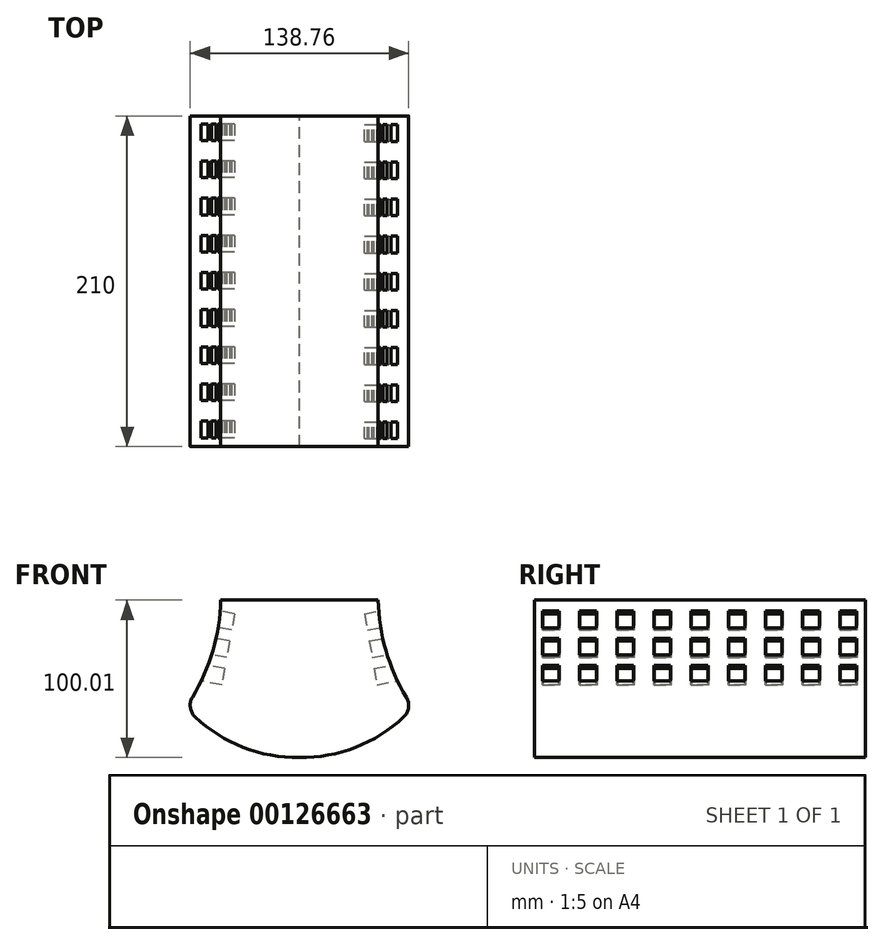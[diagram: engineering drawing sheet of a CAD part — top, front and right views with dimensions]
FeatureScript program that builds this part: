
annotation { "Feature Type Name" : "Feature", "Feature Type Description" : "" }
export const myFeature = defineFeature(function(context is Context, id is Id, definition is map)
    precondition{}
    {
        {
            var Q0;
            Q0=qCreatedBy(makeId("Front.planeOp"),FACE);
            var sketch = newSketch(context, id + "F0", { "sketchPlane" : qUnion([Q0])});
            skLineSegment(sketch, "E0", {"start": v(0, 100) * mm, "end": v(50, 100) * mm});
            skArc(sketch, "E1", {"start": v(50, 100) * mm, "mid": v(56.03, 64.31) * mm, "end": v(72.09, 31.88) * mm});
            skArc(sketch, "E2", {"start": v(0, 0) * mm, "mid": v(39.53, 8.06) * mm, "end": v(72.09, 31.88) * mm});
            skLineSegment(sketch, "E3", {"start": v(0, 100) * mm, "end": v(-50, 100) * mm});
            skArc(sketch, "E4", {"start": v(-72.09, 31.88) * mm, "mid": v(-56.03, 64.31) * mm, "end": v(-50, 100) * mm});
            skArc(sketch, "E5", {"start": v(-72.09, 31.88) * mm, "mid": v(-39.53, 8.06) * mm, "end": v(0, 0) * mm});
            skSolve(sketch);
        }
        {
            var Q0;
            Q0=makeQuery(id+"F0.imprint","IMPRINT",FACE,{"disambiguationData":[TD([[makeQuery(id+"F0.imprint","IMPRINT",EDGE,{"derivedFrom":sQuery(id+"F0.wireOp",EDGE,"E0")}),-1.0]])]});
            extrude(context, id + "F1", {"entities" : qUnion([Q0]), "depth" : 205 * mm, "hasSecondDirection" : true, "secondDirectionOppositeDirection" : true, "secondDirectionDepth" : 5 * mm});
        }
        {
            var Q0;
            Q0=makeQuery(id+"F1.opExtrude","SWEPT_EDGE",EDGE,{"disambiguationData":[OSD([sQuery(id+"F0.wireOp",EDGE,"E1"),sQuery(id+"F0.wireOp",EDGE,"E2")])]});
            cPlane(context, id + "F2", {"entities" : qUnion([Q0]), "cplaneType" : CPlaneType.LINE_ANGLE, "offset" : 25 * mm, "angle" : 80 * degree, "width" : 150 * mm, "height" : 150 * mm});
        }
        {
            var Q0;
            Q0=qCreatedBy(id+"F2.planeOp",FACE);
            var sketch = newSketch(context, id + "F3", { "sketchPlane" : qUnion([Q0])});
            skLineSegment(sketch, "E6", {"start": v(0, 89.8) * mm, "end": v(-200, 89.8) * mm});
            skLineSegment(sketch, "E7.bottom", {"start": v(-200, 89.8) * mm, "end": v(0, 89.8) * mm});
            skLineSegment(sketch, "E7.right", {"start": v(0, 89.8) * mm, "end": v(0, 82.8) * mm});
            skLineSegment(sketch, "E8.bottom", {"start": v(-200, 82.8) * mm, "end": v(-189.4, 82.8) * mm});
            skLineSegment(sketch, "E8.top", {"start": v(-200, 72.2) * mm, "end": v(-189.4, 72.2) * mm});
            skLineSegment(sketch, "E8.left", {"start": v(-200, 82.8) * mm, "end": v(-200, 72.2) * mm});
            skLineSegment(sketch, "E8.right", {"start": v(-189.4, 82.8) * mm, "end": v(-189.4, 72.2) * mm});
            skLineSegment(sketch, "E9", {"start": v(-200, 89.8) * mm, "end": v(-200, 82.8) * mm});
            skLineSegment(sketch, "E10.bottom", {"start": v(-176.4, 82.8) * mm, "end": v(-165.8, 82.8) * mm});
            skLineSegment(sketch, "E10.top", {"start": v(-176.4, 72.2) * mm, "end": v(-165.8, 72.2) * mm});
            skLineSegment(sketch, "E10.left", {"start": v(-176.4, 82.8) * mm, "end": v(-176.4, 72.2) * mm});
            skLineSegment(sketch, "E10.right", {"start": v(-165.8, 82.8) * mm, "end": v(-165.8, 72.2) * mm});
            skLineSegment(sketch, "E11.bottom", {"start": v(-152.8, 82.8) * mm, "end": v(-142.2, 82.8) * mm});
            skLineSegment(sketch, "E11.top", {"start": v(-152.8, 72.2) * mm, "end": v(-142.2, 72.2) * mm});
            skLineSegment(sketch, "E11.left", {"start": v(-152.8, 82.8) * mm, "end": v(-152.8, 72.2) * mm});
            skLineSegment(sketch, "E11.right", {"start": v(-142.2, 82.8) * mm, "end": v(-142.2, 72.2) * mm});
            skLineSegment(sketch, "E12.bottom", {"start": v(-129.2, 82.8) * mm, "end": v(-118.6, 82.8) * mm});
            skLineSegment(sketch, "E12.top", {"start": v(-129.2, 72.2) * mm, "end": v(-118.6, 72.2) * mm});
            skLineSegment(sketch, "E12.left", {"start": v(-129.2, 82.8) * mm, "end": v(-129.2, 72.2) * mm});
            skLineSegment(sketch, "E12.right", {"start": v(-118.6, 82.8) * mm, "end": v(-118.6, 72.2) * mm});
            skLineSegment(sketch, "E13", {"start": v(-189.4, 82.8) * mm, "end": v(-176.4, 82.8) * mm});
            skLineSegment(sketch, "E14", {"start": v(-165.8, 82.8) * mm, "end": v(-152.8, 82.8) * mm});
            skLineSegment(sketch, "E15", {"start": v(-142.2, 82.8) * mm, "end": v(-129.2, 82.8) * mm});
            skLineSegment(sketch, "E16", {"start": v(-118.6, 82.8) * mm, "end": v(-105.6, 82.8) * mm});
            skLineSegment(sketch, "E17.bottom", {"start": v(-105.6, 82.8) * mm, "end": v(-95, 82.8) * mm});
            skLineSegment(sketch, "E17.top", {"start": v(-105.6, 72.2) * mm, "end": v(-95, 72.2) * mm});
            skLineSegment(sketch, "E17.left", {"start": v(-105.6, 82.8) * mm, "end": v(-105.6, 72.2) * mm});
            skLineSegment(sketch, "E17.right", {"start": v(-95, 82.8) * mm, "end": v(-95, 72.2) * mm});
            skLineSegment(sketch, "E18.bottom", {"start": v(-82, 82.8) * mm, "end": v(-71.4, 82.8) * mm});
            skLineSegment(sketch, "E18.top", {"start": v(-82, 72.2) * mm, "end": v(-71.4, 72.2) * mm});
            skLineSegment(sketch, "E18.left", {"start": v(-82, 82.8) * mm, "end": v(-82, 72.2) * mm});
            skLineSegment(sketch, "E18.right", {"start": v(-71.4, 82.8) * mm, "end": v(-71.4, 72.2) * mm});
            skLineSegment(sketch, "E19", {"start": v(-95, 82.8) * mm, "end": v(-82, 82.8) * mm});
            skLineSegment(sketch, "E20", {"start": v(-71.4, 82.8) * mm, "end": v(-58.4, 82.8) * mm});
            skLineSegment(sketch, "E21.bottom", {"start": v(-58.4, 82.8) * mm, "end": v(-47.8, 82.8) * mm});
            skLineSegment(sketch, "E21.top", {"start": v(-58.4, 72.2) * mm, "end": v(-47.8, 72.2) * mm});
            skLineSegment(sketch, "E21.left", {"start": v(-58.4, 82.8) * mm, "end": v(-58.4, 72.2) * mm});
            skLineSegment(sketch, "E21.right", {"start": v(-47.8, 82.8) * mm, "end": v(-47.8, 72.2) * mm});
            skLineSegment(sketch, "E22", {"start": v(-47.8, 82.8) * mm, "end": v(-34.8, 82.8) * mm});
            skLineSegment(sketch, "E23.bottom", {"start": v(-34.8, 82.8) * mm, "end": v(-24.2, 82.8) * mm});
            skLineSegment(sketch, "E23.top", {"start": v(-34.8, 72.2) * mm, "end": v(-24.2, 72.2) * mm});
            skLineSegment(sketch, "E23.left", {"start": v(-34.8, 82.8) * mm, "end": v(-34.8, 72.2) * mm});
            skLineSegment(sketch, "E23.right", {"start": v(-24.2, 82.8) * mm, "end": v(-24.2, 72.2) * mm});
            skLineSegment(sketch, "E24", {"start": v(-24.2, 82.8) * mm, "end": v(-11.2, 82.8) * mm});
            skLineSegment(sketch, "E25.bottom", {"start": v(-11.2, 82.8) * mm, "end": v(-0.6, 82.8) * mm});
            skLineSegment(sketch, "E25.top", {"start": v(-11.2, 72.2) * mm, "end": v(-0.6, 72.2) * mm});
            skLineSegment(sketch, "E25.left", {"start": v(-11.2, 82.8) * mm, "end": v(-11.2, 72.2) * mm});
            skLineSegment(sketch, "E25.right", {"start": v(-0.6, 82.8) * mm, "end": v(-0.6, 72.2) * mm});
            skLineSegment(sketch, "E26", {"start": v(-0.6, 82.8) * mm, "end": v(0, 82.8) * mm});
            skLineSegment(sketch, "E27", {"start": v(-200, 72.2) * mm, "end": v(-200, 65.2) * mm});
            skLineSegment(sketch, "E28", {"start": v(-200, 65.2) * mm, "end": v(-200, 54.6) * mm});
            skLineSegment(sketch, "E29", {"start": v(-200, 54.6) * mm, "end": v(-200, 47.6) * mm});
            skLineSegment(sketch, "E30", {"start": v(-200, 47.6) * mm, "end": v(-200, 37) * mm});
            skLineSegment(sketch, "E31.bottom", {"start": v(-200, 65.2) * mm, "end": v(-189.4, 65.2) * mm});
            skLineSegment(sketch, "E31.top", {"start": v(-200, 54.6) * mm, "end": v(-189.4, 54.6) * mm});
            skLineSegment(sketch, "E31.right", {"start": v(-189.4, 65.2) * mm, "end": v(-189.4, 54.6) * mm});
            skLineSegment(sketch, "E32.bottom", {"start": v(-200, 47.6) * mm, "end": v(-189.4, 47.6) * mm});
            skLineSegment(sketch, "E32.top", {"start": v(-200, 37) * mm, "end": v(-189.4, 37) * mm});
            skLineSegment(sketch, "E32.right", {"start": v(-189.4, 47.6) * mm, "end": v(-189.4, 37) * mm});
            skLineSegment(sketch, "E33.bottom", {"start": v(-176.4, 65.2) * mm, "end": v(-165.8, 65.2) * mm});
            skLineSegment(sketch, "E33.top", {"start": v(-176.4, 54.6) * mm, "end": v(-165.8, 54.6) * mm});
            skLineSegment(sketch, "E33.left", {"start": v(-176.4, 65.2) * mm, "end": v(-176.4, 54.6) * mm});
            skLineSegment(sketch, "E33.right", {"start": v(-165.8, 65.2) * mm, "end": v(-165.8, 54.6) * mm});
            skLineSegment(sketch, "E34.bottom", {"start": v(-152.8, 65.2) * mm, "end": v(-142.2, 65.2) * mm});
            skLineSegment(sketch, "E34.top", {"start": v(-152.8, 54.6) * mm, "end": v(-142.2, 54.6) * mm});
            skLineSegment(sketch, "E34.left", {"start": v(-152.8, 65.2) * mm, "end": v(-152.8, 54.6) * mm});
            skLineSegment(sketch, "E34.right", {"start": v(-142.2, 65.2) * mm, "end": v(-142.2, 54.6) * mm});
            skLineSegment(sketch, "E35.bottom", {"start": v(-129.2, 65.2) * mm, "end": v(-118.6, 65.2) * mm});
            skLineSegment(sketch, "E35.top", {"start": v(-129.2, 54.6) * mm, "end": v(-118.6, 54.6) * mm});
            skLineSegment(sketch, "E35.left", {"start": v(-129.2, 65.2) * mm, "end": v(-129.2, 54.6) * mm});
            skLineSegment(sketch, "E35.right", {"start": v(-118.6, 65.2) * mm, "end": v(-118.6, 54.6) * mm});
            skLineSegment(sketch, "E36.bottom", {"start": v(-105.6, 65.2) * mm, "end": v(-95, 65.2) * mm});
            skLineSegment(sketch, "E36.top", {"start": v(-105.6, 54.6) * mm, "end": v(-95, 54.6) * mm});
            skLineSegment(sketch, "E36.left", {"start": v(-105.6, 65.2) * mm, "end": v(-105.6, 54.6) * mm});
            skLineSegment(sketch, "E36.right", {"start": v(-95, 65.2) * mm, "end": v(-95, 54.6) * mm});
            skLineSegment(sketch, "E37.bottom", {"start": v(-82, 65.2) * mm, "end": v(-71.4, 65.2) * mm});
            skLineSegment(sketch, "E37.top", {"start": v(-82, 54.6) * mm, "end": v(-71.4, 54.6) * mm});
            skLineSegment(sketch, "E37.left", {"start": v(-82, 65.2) * mm, "end": v(-82, 54.6) * mm});
            skLineSegment(sketch, "E37.right", {"start": v(-71.4, 65.2) * mm, "end": v(-71.4, 54.6) * mm});
            skLineSegment(sketch, "E38.bottom", {"start": v(-58.4, 65.2) * mm, "end": v(-47.8, 65.2) * mm});
            skLineSegment(sketch, "E38.top", {"start": v(-58.4, 54.6) * mm, "end": v(-47.8, 54.6) * mm});
            skLineSegment(sketch, "E38.left", {"start": v(-58.4, 65.2) * mm, "end": v(-58.4, 54.6) * mm});
            skLineSegment(sketch, "E38.right", {"start": v(-47.8, 65.2) * mm, "end": v(-47.8, 54.6) * mm});
            skLineSegment(sketch, "E39.bottom", {"start": v(-34.8, 65.2) * mm, "end": v(-24.2, 65.2) * mm});
            skLineSegment(sketch, "E39.top", {"start": v(-34.8, 54.6) * mm, "end": v(-24.2, 54.6) * mm});
            skLineSegment(sketch, "E39.left", {"start": v(-34.8, 65.2) * mm, "end": v(-34.8, 54.6) * mm});
            skLineSegment(sketch, "E39.right", {"start": v(-24.2, 65.2) * mm, "end": v(-24.2, 54.6) * mm});
            skLineSegment(sketch, "E40.bottom", {"start": v(-11.2, 65.2) * mm, "end": v(-0.6, 65.2) * mm});
            skLineSegment(sketch, "E40.top", {"start": v(-11.2, 54.6) * mm, "end": v(-0.6, 54.6) * mm});
            skLineSegment(sketch, "E40.left", {"start": v(-11.2, 65.2) * mm, "end": v(-11.2, 54.6) * mm});
            skLineSegment(sketch, "E40.right", {"start": v(-0.6, 65.2) * mm, "end": v(-0.6, 54.6) * mm});
            skLineSegment(sketch, "E41", {"start": v(-189.4, 65.2) * mm, "end": v(-176.4, 65.2) * mm});
            skLineSegment(sketch, "E42", {"start": v(-165.8, 65.2) * mm, "end": v(-152.8, 65.2) * mm});
            skLineSegment(sketch, "E43", {"start": v(-142.2, 65.2) * mm, "end": v(-129.2, 65.2) * mm});
            skLineSegment(sketch, "E44", {"start": v(-118.6, 65.2) * mm, "end": v(-105.6, 65.2) * mm});
            skLineSegment(sketch, "E45", {"start": v(-95, 65.2) * mm, "end": v(-82, 65.2) * mm});
            skLineSegment(sketch, "E46", {"start": v(-71.4, 65.2) * mm, "end": v(-58.4, 65.2) * mm});
            skLineSegment(sketch, "E47", {"start": v(-47.8, 65.2) * mm, "end": v(-34.8, 65.2) * mm});
            skLineSegment(sketch, "E48", {"start": v(-24.2, 65.2) * mm, "end": v(-11.2, 65.2) * mm});
            skLineSegment(sketch, "E49.bottom", {"start": v(-176.4, 47.6) * mm, "end": v(-165.8, 47.6) * mm});
            skLineSegment(sketch, "E49.top", {"start": v(-176.4, 37) * mm, "end": v(-165.8, 37) * mm});
            skLineSegment(sketch, "E49.left", {"start": v(-176.4, 47.6) * mm, "end": v(-176.4, 37) * mm});
            skLineSegment(sketch, "E49.right", {"start": v(-165.8, 47.6) * mm, "end": v(-165.8, 37) * mm});
            skLineSegment(sketch, "E50.bottom", {"start": v(-152.8, 47.6) * mm, "end": v(-142.2, 47.6) * mm});
            skLineSegment(sketch, "E50.top", {"start": v(-152.8, 37) * mm, "end": v(-142.2, 37) * mm});
            skLineSegment(sketch, "E50.left", {"start": v(-152.8, 47.6) * mm, "end": v(-152.8, 37) * mm});
            skLineSegment(sketch, "E50.right", {"start": v(-142.2, 47.6) * mm, "end": v(-142.2, 37) * mm});
            skLineSegment(sketch, "E51.bottom", {"start": v(-129.2, 47.6) * mm, "end": v(-118.6, 47.6) * mm});
            skLineSegment(sketch, "E51.top", {"start": v(-129.2, 37) * mm, "end": v(-118.6, 37) * mm});
            skLineSegment(sketch, "E51.left", {"start": v(-129.2, 47.6) * mm, "end": v(-129.2, 37) * mm});
            skLineSegment(sketch, "E51.right", {"start": v(-118.6, 47.6) * mm, "end": v(-118.6, 37) * mm});
            skLineSegment(sketch, "E52.bottom", {"start": v(-105.6, 47.6) * mm, "end": v(-95, 47.6) * mm});
            skLineSegment(sketch, "E52.top", {"start": v(-105.6, 37) * mm, "end": v(-95, 37) * mm});
            skLineSegment(sketch, "E52.left", {"start": v(-105.6, 47.6) * mm, "end": v(-105.6, 37) * mm});
            skLineSegment(sketch, "E52.right", {"start": v(-95, 47.6) * mm, "end": v(-95, 37) * mm});
            skLineSegment(sketch, "E53.bottom", {"start": v(-82, 47.6) * mm, "end": v(-71.4, 47.6) * mm});
            skLineSegment(sketch, "E53.top", {"start": v(-82, 37) * mm, "end": v(-71.4, 37) * mm});
            skLineSegment(sketch, "E53.left", {"start": v(-82, 47.6) * mm, "end": v(-82, 37) * mm});
            skLineSegment(sketch, "E53.right", {"start": v(-71.4, 47.6) * mm, "end": v(-71.4, 37) * mm});
            skLineSegment(sketch, "E54.bottom", {"start": v(-58.4, 47.6) * mm, "end": v(-47.8, 47.6) * mm});
            skLineSegment(sketch, "E54.top", {"start": v(-58.4, 37) * mm, "end": v(-47.8, 37) * mm});
            skLineSegment(sketch, "E54.left", {"start": v(-58.4, 47.6) * mm, "end": v(-58.4, 37) * mm});
            skLineSegment(sketch, "E54.right", {"start": v(-47.8, 47.6) * mm, "end": v(-47.8, 37) * mm});
            skLineSegment(sketch, "E55.bottom", {"start": v(-34.8, 47.6) * mm, "end": v(-24.2, 47.6) * mm});
            skLineSegment(sketch, "E55.top", {"start": v(-34.8, 37) * mm, "end": v(-24.2, 37) * mm});
            skLineSegment(sketch, "E55.left", {"start": v(-34.8, 47.6) * mm, "end": v(-34.8, 37) * mm});
            skLineSegment(sketch, "E55.right", {"start": v(-24.2, 47.6) * mm, "end": v(-24.2, 37) * mm});
            skLineSegment(sketch, "E56.bottom", {"start": v(-11.2, 47.6) * mm, "end": v(-0.6, 47.6) * mm});
            skLineSegment(sketch, "E56.top", {"start": v(-11.2, 37) * mm, "end": v(-0.6, 37) * mm});
            skLineSegment(sketch, "E56.left", {"start": v(-11.2, 47.6) * mm, "end": v(-11.2, 37) * mm});
            skLineSegment(sketch, "E56.right", {"start": v(-0.6, 47.6) * mm, "end": v(-0.6, 37) * mm});
            skLineSegment(sketch, "E57", {"start": v(-189.4, 47.6) * mm, "end": v(-176.4, 47.6) * mm});
            skLineSegment(sketch, "E58", {"start": v(-165.8, 47.6) * mm, "end": v(-152.8, 47.6) * mm});
            skLineSegment(sketch, "E59", {"start": v(-142.2, 47.6) * mm, "end": v(-129.2, 47.6) * mm});
            skLineSegment(sketch, "E60", {"start": v(-118.6, 47.6) * mm, "end": v(-105.6, 47.6) * mm});
            skLineSegment(sketch, "E61", {"start": v(-95, 47.6) * mm, "end": v(-82, 47.6) * mm});
            skLineSegment(sketch, "E62", {"start": v(-71.4, 47.6) * mm, "end": v(-58.4, 47.6) * mm});
            skLineSegment(sketch, "E63", {"start": v(-47.8, 47.6) * mm, "end": v(-34.8, 47.6) * mm});
            skLineSegment(sketch, "E64", {"start": v(-24.2, 47.6) * mm, "end": v(-11.2, 47.6) * mm});
            skLineSegment(sketch, "E65", {"start": v(-200, 89.8) * mm, "end": v(-205, 89.8) * mm});
            skSolve(sketch);
        }
        {
            var Q0;
            Q0=makeQuery(id+"F3.imprint","IMPRINT",FACE,{"disambiguationData":[TD([[makeQuery(id+"F3.imprint","IMPRINT",EDGE,{"derivedFrom":sQuery(id+"F3.wireOp",EDGE,"E8.bottom")}),-1.0]])]});
            var Q1;
            Q1=makeQuery(id+"F3.imprint","IMPRINT",FACE,{"disambiguationData":[TD([[makeQuery(id+"F3.imprint","IMPRINT",EDGE,{"derivedFrom":sQuery(id+"F3.wireOp",EDGE,"E10.bottom")}),-1.0]])]});
            var Q2;
            Q2=makeQuery(id+"F3.imprint","IMPRINT",FACE,{"disambiguationData":[TD([[makeQuery(id+"F3.imprint","IMPRINT",EDGE,{"derivedFrom":sQuery(id+"F3.wireOp",EDGE,"E11.bottom")}),-1.0]])]});
            var Q3;
            Q3=makeQuery(id+"F3.imprint","IMPRINT",FACE,{"disambiguationData":[TD([[makeQuery(id+"F3.imprint","IMPRINT",EDGE,{"derivedFrom":sQuery(id+"F3.wireOp",EDGE,"E12.bottom")}),-1.0]])]});
            var Q4;
            Q4=makeQuery(id+"F3.imprint","IMPRINT",FACE,{"disambiguationData":[TD([[makeQuery(id+"F3.imprint","IMPRINT",EDGE,{"derivedFrom":sQuery(id+"F3.wireOp",EDGE,"E17.bottom")}),-1.0]])]});
            var Q5;
            Q5=makeQuery(id+"F3.imprint","IMPRINT",FACE,{"disambiguationData":[TD([[makeQuery(id+"F3.imprint","IMPRINT",EDGE,{"derivedFrom":sQuery(id+"F3.wireOp",EDGE,"E18.bottom")}),-1.0]])]});
            var Q6;
            Q6=makeQuery(id+"F3.imprint","IMPRINT",FACE,{"disambiguationData":[TD([[makeQuery(id+"F3.imprint","IMPRINT",EDGE,{"derivedFrom":sQuery(id+"F3.wireOp",EDGE,"E21.bottom")}),-1.0]])]});
            var Q7;
            Q7=makeQuery(id+"F3.imprint","IMPRINT",FACE,{"disambiguationData":[TD([[makeQuery(id+"F3.imprint","IMPRINT",EDGE,{"derivedFrom":sQuery(id+"F3.wireOp",EDGE,"E23.bottom")}),-1.0]])]});
            var Q8;
            Q8=makeQuery(id+"F3.imprint","IMPRINT",FACE,{"disambiguationData":[TD([[makeQuery(id+"F3.imprint","IMPRINT",EDGE,{"derivedFrom":sQuery(id+"F3.wireOp",EDGE,"E25.bottom")}),-1.0]])]});
            var Q9;
            Q9=makeQuery(id+"F3.imprint","IMPRINT",FACE,{"disambiguationData":[TD([[makeQuery(id+"F3.imprint","IMPRINT",EDGE,{"derivedFrom":sQuery(id+"F3.wireOp",EDGE,"E40.bottom")}),-1.0]])]});
            var Q10;
            Q10=makeQuery(id+"F3.imprint","IMPRINT",FACE,{"disambiguationData":[TD([[makeQuery(id+"F3.imprint","IMPRINT",EDGE,{"derivedFrom":sQuery(id+"F3.wireOp",EDGE,"E39.bottom")}),-1.0]])]});
            var Q11;
            Q11=makeQuery(id+"F3.imprint","IMPRINT",FACE,{"disambiguationData":[TD([[makeQuery(id+"F3.imprint","IMPRINT",EDGE,{"derivedFrom":sQuery(id+"F3.wireOp",EDGE,"E38.bottom")}),-1.0]])]});
            var Q12;
            Q12=makeQuery(id+"F3.imprint","IMPRINT",FACE,{"disambiguationData":[TD([[makeQuery(id+"F3.imprint","IMPRINT",EDGE,{"derivedFrom":sQuery(id+"F3.wireOp",EDGE,"E37.bottom")}),-1.0]])]});
            var Q13;
            Q13=makeQuery(id+"F3.imprint","IMPRINT",FACE,{"disambiguationData":[TD([[makeQuery(id+"F3.imprint","IMPRINT",EDGE,{"derivedFrom":sQuery(id+"F3.wireOp",EDGE,"E36.bottom")}),-1.0]])]});
            var Q14;
            Q14=makeQuery(id+"F3.imprint","IMPRINT",FACE,{"disambiguationData":[TD([[makeQuery(id+"F3.imprint","IMPRINT",EDGE,{"derivedFrom":sQuery(id+"F3.wireOp",EDGE,"E35.bottom")}),-1.0]])]});
            var Q15;
            Q15=makeQuery(id+"F3.imprint","IMPRINT",FACE,{"disambiguationData":[TD([[makeQuery(id+"F3.imprint","IMPRINT",EDGE,{"derivedFrom":sQuery(id+"F3.wireOp",EDGE,"E34.bottom")}),-1.0]])]});
            var Q16;
            Q16=makeQuery(id+"F3.imprint","IMPRINT",FACE,{"disambiguationData":[TD([[makeQuery(id+"F3.imprint","IMPRINT",EDGE,{"derivedFrom":sQuery(id+"F3.wireOp",EDGE,"E33.bottom")}),-1.0]])]});
            var Q17;
            Q17=makeQuery(id+"F3.imprint","IMPRINT",FACE,{"disambiguationData":[TD([[makeQuery(id+"F3.imprint","IMPRINT",EDGE,{"derivedFrom":sQuery(id+"F3.wireOp",EDGE,"E31.bottom")}),-1.0]])]});
            var Q18;
            Q18=makeQuery(id+"F3.imprint","IMPRINT",FACE,{"disambiguationData":[TD([[makeQuery(id+"F3.imprint","IMPRINT",EDGE,{"derivedFrom":sQuery(id+"F3.wireOp",EDGE,"E32.bottom")}),-1.0]])]});
            var Q19;
            Q19=makeQuery(id+"F3.imprint","IMPRINT",FACE,{"disambiguationData":[TD([[makeQuery(id+"F3.imprint","IMPRINT",EDGE,{"derivedFrom":sQuery(id+"F3.wireOp",EDGE,"E49.bottom")}),-1.0]])]});
            var Q20;
            Q20=makeQuery(id+"F3.imprint","IMPRINT",FACE,{"disambiguationData":[TD([[makeQuery(id+"F3.imprint","IMPRINT",EDGE,{"derivedFrom":sQuery(id+"F3.wireOp",EDGE,"E50.bottom")}),-1.0]])]});
            var Q21;
            Q21=makeQuery(id+"F3.imprint","IMPRINT",FACE,{"disambiguationData":[TD([[makeQuery(id+"F3.imprint","IMPRINT",EDGE,{"derivedFrom":sQuery(id+"F3.wireOp",EDGE,"E51.bottom")}),-1.0]])]});
            var Q22;
            Q22=makeQuery(id+"F3.imprint","IMPRINT",FACE,{"disambiguationData":[TD([[makeQuery(id+"F3.imprint","IMPRINT",EDGE,{"derivedFrom":sQuery(id+"F3.wireOp",EDGE,"E52.bottom")}),-1.0]])]});
            var Q23;
            Q23=makeQuery(id+"F3.imprint","IMPRINT",FACE,{"disambiguationData":[TD([[makeQuery(id+"F3.imprint","IMPRINT",EDGE,{"derivedFrom":sQuery(id+"F3.wireOp",EDGE,"E53.bottom")}),-1.0]])]});
            var Q24;
            Q24=makeQuery(id+"F3.imprint","IMPRINT",FACE,{"disambiguationData":[TD([[makeQuery(id+"F3.imprint","IMPRINT",EDGE,{"derivedFrom":sQuery(id+"F3.wireOp",EDGE,"E54.bottom")}),-1.0]])]});
            var Q25;
            Q25=makeQuery(id+"F3.imprint","IMPRINT",FACE,{"disambiguationData":[TD([[makeQuery(id+"F3.imprint","IMPRINT",EDGE,{"derivedFrom":sQuery(id+"F3.wireOp",EDGE,"E55.bottom")}),-1.0]])]});
            var Q26;
            Q26=makeQuery(id+"F3.imprint","IMPRINT",FACE,{"disambiguationData":[TD([[makeQuery(id+"F3.imprint","IMPRINT",EDGE,{"derivedFrom":sQuery(id+"F3.wireOp",EDGE,"E56.bottom")}),-1.0]])]});
            extrude(context, id + "F4", {"entities" : qUnion([Q0, Q1, Q2, Q3, Q4, Q5, Q6, Q7, Q8, Q9, Q10, Q11, Q12, Q13, Q14, Q15, Q16, Q17, Q18, Q19, Q20, Q21, Q22, Q23, Q24, Q25, Q26]), "operationType" : NewBodyOperationType.REMOVE, "oppositeDirection" : true, "depth" : 20 * mm});
        }
        {
            var Q0;
            Q0=makeQuery(id+"F1.opExtrude","SWEPT_EDGE",EDGE,{"disambiguationData":[OSD([sQuery(id+"F0.wireOp",EDGE,"E4"),sQuery(id+"F0.wireOp",EDGE,"E5")])]});
            cPlane(context, id + "F5", {"entities" : qUnion([Q0]), "cplaneType" : CPlaneType.LINE_ANGLE, "offset" : 25 * mm, "angle" : 100 * degree, "width" : 150 * mm, "height" : 150 * mm});
        }
        {
            var Q0;
            Q0=qCreatedBy(id+"F5.planeOp",FACE);
            var sketch = newSketch(context, id + "F6", { "sketchPlane" : qUnion([Q0])});
            skLineSegment(sketch, "E66", {"start": v(5, 89.78) * mm, "end": v(0, 89.78) * mm});
            skLineSegment(sketch, "E67", {"start": v(5, 89.78) * mm, "end": v(5, 82.78) * mm});
            skLineSegment(sketch, "E68.top", {"start": v(5, 82.78) * mm, "end": v(0, 82.78) * mm});
            skLineSegment(sketch, "E68.right", {"start": v(0, 89.78) * mm, "end": v(0, 82.78) * mm});
            skLineSegment(sketch, "E69.bottom", {"start": v(-205, 89.78) * mm, "end": v(-200, 89.78) * mm});
            skLineSegment(sketch, "E69.top", {"start": v(-205, 82.78) * mm, "end": v(-200, 82.78) * mm});
            skLineSegment(sketch, "E69.left", {"start": v(-205, 89.78) * mm, "end": v(-205, 82.78) * mm});
            skLineSegment(sketch, "E69.right", {"start": v(-200, 89.78) * mm, "end": v(-200, 82.78) * mm});
            skLineSegment(sketch, "E70.bottom", {"start": v(0, 82.78) * mm, "end": v(-10.6, 82.78) * mm});
            skLineSegment(sketch, "E70.top", {"start": v(0, 72.18) * mm, "end": v(-10.6, 72.18) * mm});
            skLineSegment(sketch, "E70.right", {"start": v(-10.6, 82.78) * mm, "end": v(-10.6, 72.18) * mm});
            skLineSegment(sketch, "E71", {"start": v(0, 82.78) * mm, "end": v(0, 72.18) * mm});
            skLineSegment(sketch, "E72", {"start": v(-10.6, 82.78) * mm, "end": v(-23.6, 82.78) * mm});
            skLineSegment(sketch, "E73.bottom", {"start": v(-23.6, 82.78) * mm, "end": v(-34.2, 82.78) * mm});
            skLineSegment(sketch, "E73.top", {"start": v(-23.6, 72.18) * mm, "end": v(-34.2, 72.18) * mm});
            skLineSegment(sketch, "E73.left", {"start": v(-23.6, 82.78) * mm, "end": v(-23.6, 72.18) * mm});
            skLineSegment(sketch, "E73.right", {"start": v(-34.2, 82.78) * mm, "end": v(-34.2, 72.18) * mm});
            skLineSegment(sketch, "E74", {"start": v(-34.2, 82.78) * mm, "end": v(-47.2, 82.78) * mm});
            skLineSegment(sketch, "E75.bottom", {"start": v(-47.2, 82.78) * mm, "end": v(-57.8, 82.78) * mm});
            skLineSegment(sketch, "E75.top", {"start": v(-47.2, 72.18) * mm, "end": v(-57.8, 72.18) * mm});
            skLineSegment(sketch, "E75.left", {"start": v(-47.2, 82.78) * mm, "end": v(-47.2, 72.18) * mm});
            skLineSegment(sketch, "E75.right", {"start": v(-57.8, 82.78) * mm, "end": v(-57.8, 72.18) * mm});
            skLineSegment(sketch, "E76", {"start": v(-57.8, 82.78) * mm, "end": v(-70.8, 82.78) * mm});
            skLineSegment(sketch, "E77.bottom", {"start": v(-70.8, 82.78) * mm, "end": v(-81.4, 82.78) * mm});
            skLineSegment(sketch, "E77.top", {"start": v(-70.8, 72.18) * mm, "end": v(-81.4, 72.18) * mm});
            skLineSegment(sketch, "E77.left", {"start": v(-70.8, 82.78) * mm, "end": v(-70.8, 72.18) * mm});
            skLineSegment(sketch, "E77.right", {"start": v(-81.4, 82.78) * mm, "end": v(-81.4, 72.18) * mm});
            skLineSegment(sketch, "E78", {"start": v(-81.4, 82.78) * mm, "end": v(-94.4, 82.78) * mm});
            skLineSegment(sketch, "E79.bottom", {"start": v(-94.4, 82.78) * mm, "end": v(-105, 82.78) * mm});
            skLineSegment(sketch, "E79.top", {"start": v(-94.4, 72.18) * mm, "end": v(-105, 72.18) * mm});
            skLineSegment(sketch, "E79.left", {"start": v(-94.4, 82.78) * mm, "end": v(-94.4, 72.18) * mm});
            skLineSegment(sketch, "E79.right", {"start": v(-105, 82.78) * mm, "end": v(-105, 72.18) * mm});
            skLineSegment(sketch, "E80", {"start": v(-105, 82.78) * mm, "end": v(-118, 82.78) * mm});
            skLineSegment(sketch, "E81.bottom", {"start": v(-118, 82.78) * mm, "end": v(-128.6, 82.78) * mm});
            skLineSegment(sketch, "E81.top", {"start": v(-118, 72.18) * mm, "end": v(-128.6, 72.18) * mm});
            skLineSegment(sketch, "E81.left", {"start": v(-118, 82.78) * mm, "end": v(-118, 72.18) * mm});
            skLineSegment(sketch, "E81.right", {"start": v(-128.6, 82.78) * mm, "end": v(-128.6, 72.18) * mm});
            skLineSegment(sketch, "E82", {"start": v(-128.6, 82.78) * mm, "end": v(-141.6, 82.78) * mm});
            skLineSegment(sketch, "E83.bottom", {"start": v(-141.6, 82.78) * mm, "end": v(-152.2, 82.78) * mm});
            skLineSegment(sketch, "E83.top", {"start": v(-141.6, 72.18) * mm, "end": v(-152.2, 72.18) * mm});
            skLineSegment(sketch, "E83.left", {"start": v(-141.6, 82.78) * mm, "end": v(-141.6, 72.18) * mm});
            skLineSegment(sketch, "E83.right", {"start": v(-152.2, 82.78) * mm, "end": v(-152.2, 72.18) * mm});
            skLineSegment(sketch, "E84", {"start": v(-152.2, 82.78) * mm, "end": v(-165.2, 82.78) * mm});
            skLineSegment(sketch, "E85.bottom", {"start": v(-165.2, 82.78) * mm, "end": v(-175.8, 82.78) * mm});
            skLineSegment(sketch, "E85.top", {"start": v(-165.2, 72.18) * mm, "end": v(-175.8, 72.18) * mm});
            skLineSegment(sketch, "E85.left", {"start": v(-165.2, 82.78) * mm, "end": v(-165.2, 72.18) * mm});
            skLineSegment(sketch, "E85.right", {"start": v(-175.8, 82.78) * mm, "end": v(-175.8, 72.18) * mm});
            skLineSegment(sketch, "E86", {"start": v(-175.8, 82.78) * mm, "end": v(-188.8, 82.78) * mm});
            skLineSegment(sketch, "E87.bottom", {"start": v(-188.8, 82.78) * mm, "end": v(-199.4, 82.78) * mm});
            skLineSegment(sketch, "E87.top", {"start": v(-188.8, 72.18) * mm, "end": v(-199.4, 72.18) * mm});
            skLineSegment(sketch, "E87.left", {"start": v(-188.8, 82.78) * mm, "end": v(-188.8, 72.18) * mm});
            skLineSegment(sketch, "E87.right", {"start": v(-199.4, 82.78) * mm, "end": v(-199.4, 72.18) * mm});
            skLineSegment(sketch, "E88", {"start": v(-199.4, 82.78) * mm, "end": v(-200, 82.78) * mm});
            skLineSegment(sketch, "E89", {"start": v(0, 72.18) * mm, "end": v(0, 65.18) * mm});
            skLineSegment(sketch, "E90", {"start": v(-199.4, 72.18) * mm, "end": v(-199.4, 65.18) * mm});
            skLineSegment(sketch, "E91.bottom", {"start": v(0, 65.18) * mm, "end": v(-10.6, 65.18) * mm});
            skLineSegment(sketch, "E91.top", {"start": v(0, 54.58) * mm, "end": v(-10.6, 54.58) * mm});
            skLineSegment(sketch, "E91.left", {"start": v(0, 65.18) * mm, "end": v(0, 54.58) * mm});
            skLineSegment(sketch, "E91.right", {"start": v(-10.6, 65.18) * mm, "end": v(-10.6, 54.58) * mm});
            skLineSegment(sketch, "E92", {"start": v(-10.6, 65.18) * mm, "end": v(-23.6, 65.18) * mm});
            skLineSegment(sketch, "E93.bottom", {"start": v(-23.6, 65.18) * mm, "end": v(-34.2, 65.18) * mm});
            skLineSegment(sketch, "E93.top", {"start": v(-23.6, 54.58) * mm, "end": v(-34.2, 54.58) * mm});
            skLineSegment(sketch, "E93.left", {"start": v(-23.6, 65.18) * mm, "end": v(-23.6, 54.58) * mm});
            skLineSegment(sketch, "E93.right", {"start": v(-34.2, 65.18) * mm, "end": v(-34.2, 54.58) * mm});
            skLineSegment(sketch, "E94", {"start": v(-34.2, 65.18) * mm, "end": v(-47.2, 65.18) * mm});
            skLineSegment(sketch, "E95.bottom", {"start": v(-47.2, 65.18) * mm, "end": v(-57.8, 65.18) * mm});
            skLineSegment(sketch, "E95.top", {"start": v(-47.2, 54.58) * mm, "end": v(-57.8, 54.58) * mm});
            skLineSegment(sketch, "E95.left", {"start": v(-47.2, 65.18) * mm, "end": v(-47.2, 54.58) * mm});
            skLineSegment(sketch, "E95.right", {"start": v(-57.8, 65.18) * mm, "end": v(-57.8, 54.58) * mm});
            skLineSegment(sketch, "E96", {"start": v(-57.8, 65.18) * mm, "end": v(-70.8, 65.18) * mm});
            skLineSegment(sketch, "E97.bottom", {"start": v(-70.8, 65.18) * mm, "end": v(-81.4, 65.18) * mm});
            skLineSegment(sketch, "E97.top", {"start": v(-70.8, 54.58) * mm, "end": v(-81.4, 54.58) * mm});
            skLineSegment(sketch, "E97.left", {"start": v(-70.8, 65.18) * mm, "end": v(-70.8, 54.58) * mm});
            skLineSegment(sketch, "E97.right", {"start": v(-81.4, 65.18) * mm, "end": v(-81.4, 54.58) * mm});
            skLineSegment(sketch, "E98", {"start": v(-81.4, 65.18) * mm, "end": v(-94.4, 65.18) * mm});
            skLineSegment(sketch, "E99.bottom", {"start": v(-94.4, 65.18) * mm, "end": v(-105, 65.18) * mm});
            skLineSegment(sketch, "E99.top", {"start": v(-94.4, 54.58) * mm, "end": v(-105, 54.58) * mm});
            skLineSegment(sketch, "E99.left", {"start": v(-94.4, 65.18) * mm, "end": v(-94.4, 54.58) * mm});
            skLineSegment(sketch, "E99.right", {"start": v(-105, 65.18) * mm, "end": v(-105, 54.58) * mm});
            skLineSegment(sketch, "E100", {"start": v(-105, 65.18) * mm, "end": v(-118, 65.18) * mm});
            skLineSegment(sketch, "E101.bottom", {"start": v(-118, 65.18) * mm, "end": v(-128.6, 65.18) * mm});
            skLineSegment(sketch, "E101.top", {"start": v(-118, 54.58) * mm, "end": v(-128.6, 54.58) * mm});
            skLineSegment(sketch, "E101.left", {"start": v(-118, 65.18) * mm, "end": v(-118, 54.58) * mm});
            skLineSegment(sketch, "E101.right", {"start": v(-128.6, 65.18) * mm, "end": v(-128.6, 54.58) * mm});
            skLineSegment(sketch, "E102", {"start": v(-128.6, 65.18) * mm, "end": v(-141.6, 65.18) * mm});
            skLineSegment(sketch, "E103.bottom", {"start": v(-141.6, 65.18) * mm, "end": v(-152.2, 65.18) * mm});
            skLineSegment(sketch, "E103.top", {"start": v(-141.6, 54.58) * mm, "end": v(-152.2, 54.58) * mm});
            skLineSegment(sketch, "E103.left", {"start": v(-141.6, 65.18) * mm, "end": v(-141.6, 54.58) * mm});
            skLineSegment(sketch, "E103.right", {"start": v(-152.2, 65.18) * mm, "end": v(-152.2, 54.58) * mm});
            skLineSegment(sketch, "E104", {"start": v(-152.2, 65.18) * mm, "end": v(-165.2, 65.18) * mm});
            skLineSegment(sketch, "E105.bottom", {"start": v(-165.2, 65.18) * mm, "end": v(-175.8, 65.18) * mm});
            skLineSegment(sketch, "E105.top", {"start": v(-165.2, 54.58) * mm, "end": v(-175.8, 54.58) * mm});
            skLineSegment(sketch, "E105.left", {"start": v(-165.2, 65.18) * mm, "end": v(-165.2, 54.58) * mm});
            skLineSegment(sketch, "E105.right", {"start": v(-175.8, 65.18) * mm, "end": v(-175.8, 54.58) * mm});
            skLineSegment(sketch, "E106", {"start": v(-175.8, 65.18) * mm, "end": v(-188.8, 65.18) * mm});
            skLineSegment(sketch, "E107.bottom", {"start": v(-188.8, 65.18) * mm, "end": v(-199.4, 65.18) * mm});
            skLineSegment(sketch, "E107.top", {"start": v(-188.8, 54.58) * mm, "end": v(-199.4, 54.58) * mm});
            skLineSegment(sketch, "E107.left", {"start": v(-188.8, 65.18) * mm, "end": v(-188.8, 54.58) * mm});
            skLineSegment(sketch, "E107.right", {"start": v(-199.4, 65.18) * mm, "end": v(-199.4, 54.58) * mm});
            skLineSegment(sketch, "E108", {"start": v(0, 54.58) * mm, "end": v(0, 47.58) * mm});
            skLineSegment(sketch, "E109.bottom", {"start": v(0, 47.58) * mm, "end": v(-10.6, 47.58) * mm});
            skLineSegment(sketch, "E109.top", {"start": v(0, 36.98) * mm, "end": v(-10.6, 36.98) * mm});
            skLineSegment(sketch, "E109.left", {"start": v(0, 47.58) * mm, "end": v(0, 36.98) * mm});
            skLineSegment(sketch, "E109.right", {"start": v(-10.6, 47.58) * mm, "end": v(-10.6, 36.98) * mm});
            skLineSegment(sketch, "E110", {"start": v(-10.6, 47.58) * mm, "end": v(-23.6, 47.58) * mm});
            skLineSegment(sketch, "E111.bottom", {"start": v(-23.6, 47.58) * mm, "end": v(-34.2, 47.58) * mm});
            skLineSegment(sketch, "E111.top", {"start": v(-23.6, 36.98) * mm, "end": v(-34.2, 36.98) * mm});
            skLineSegment(sketch, "E111.left", {"start": v(-23.6, 47.58) * mm, "end": v(-23.6, 36.98) * mm});
            skLineSegment(sketch, "E111.right", {"start": v(-34.2, 47.58) * mm, "end": v(-34.2, 36.98) * mm});
            skLineSegment(sketch, "E112", {"start": v(-34.2, 47.58) * mm, "end": v(-47.2, 47.58) * mm});
            skLineSegment(sketch, "E113.bottom", {"start": v(-47.2, 47.58) * mm, "end": v(-57.8, 47.58) * mm});
            skLineSegment(sketch, "E113.top", {"start": v(-47.2, 36.98) * mm, "end": v(-57.8, 36.98) * mm});
            skLineSegment(sketch, "E113.left", {"start": v(-47.2, 47.58) * mm, "end": v(-47.2, 36.98) * mm});
            skLineSegment(sketch, "E113.right", {"start": v(-57.8, 47.58) * mm, "end": v(-57.8, 36.98) * mm});
            skLineSegment(sketch, "E114", {"start": v(-57.8, 47.58) * mm, "end": v(-70.8, 47.58) * mm});
            skLineSegment(sketch, "E115.bottom", {"start": v(-70.8, 47.58) * mm, "end": v(-81.4, 47.58) * mm});
            skLineSegment(sketch, "E115.top", {"start": v(-70.8, 36.98) * mm, "end": v(-81.4, 36.98) * mm});
            skLineSegment(sketch, "E115.left", {"start": v(-70.8, 47.58) * mm, "end": v(-70.8, 36.98) * mm});
            skLineSegment(sketch, "E115.right", {"start": v(-81.4, 47.58) * mm, "end": v(-81.4, 36.98) * mm});
            skLineSegment(sketch, "E116", {"start": v(-81.4, 47.58) * mm, "end": v(-94.4, 47.58) * mm});
            skLineSegment(sketch, "E117.bottom", {"start": v(-94.4, 47.58) * mm, "end": v(-105, 47.58) * mm});
            skLineSegment(sketch, "E117.top", {"start": v(-94.4, 36.98) * mm, "end": v(-105, 36.98) * mm});
            skLineSegment(sketch, "E117.left", {"start": v(-94.4, 47.58) * mm, "end": v(-94.4, 36.98) * mm});
            skLineSegment(sketch, "E117.right", {"start": v(-105, 47.58) * mm, "end": v(-105, 36.98) * mm});
            skLineSegment(sketch, "E118", {"start": v(-105, 47.58) * mm, "end": v(-118, 47.58) * mm});
            skLineSegment(sketch, "E119.bottom", {"start": v(-118, 47.58) * mm, "end": v(-128.6, 47.58) * mm});
            skLineSegment(sketch, "E119.top", {"start": v(-118, 36.98) * mm, "end": v(-128.6, 36.98) * mm});
            skLineSegment(sketch, "E119.left", {"start": v(-118, 47.58) * mm, "end": v(-118, 36.98) * mm});
            skLineSegment(sketch, "E119.right", {"start": v(-128.6, 47.58) * mm, "end": v(-128.6, 36.98) * mm});
            skLineSegment(sketch, "E120", {"start": v(-128.6, 47.58) * mm, "end": v(-141.6, 47.58) * mm});
            skLineSegment(sketch, "E121.bottom", {"start": v(-141.6, 47.58) * mm, "end": v(-152.2, 47.58) * mm});
            skLineSegment(sketch, "E121.top", {"start": v(-141.6, 36.98) * mm, "end": v(-152.2, 36.98) * mm});
            skLineSegment(sketch, "E121.left", {"start": v(-141.6, 47.58) * mm, "end": v(-141.6, 36.98) * mm});
            skLineSegment(sketch, "E121.right", {"start": v(-152.2, 47.58) * mm, "end": v(-152.2, 36.98) * mm});
            skLineSegment(sketch, "E122", {"start": v(-152.2, 47.58) * mm, "end": v(-165.2, 47.58) * mm});
            skLineSegment(sketch, "E123.bottom", {"start": v(-165.2, 47.58) * mm, "end": v(-175.8, 47.58) * mm});
            skLineSegment(sketch, "E123.top", {"start": v(-165.2, 36.98) * mm, "end": v(-175.8, 36.98) * mm});
            skLineSegment(sketch, "E123.left", {"start": v(-165.2, 47.58) * mm, "end": v(-165.2, 36.98) * mm});
            skLineSegment(sketch, "E123.right", {"start": v(-175.8, 47.58) * mm, "end": v(-175.8, 36.98) * mm});
            skLineSegment(sketch, "E124", {"start": v(-175.8, 47.58) * mm, "end": v(-188.8, 47.58) * mm});
            skLineSegment(sketch, "E125", {"start": v(-199.4, 54.58) * mm, "end": v(-199.4, 47.58) * mm});
            skLineSegment(sketch, "E126.bottom", {"start": v(-188.8, 47.58) * mm, "end": v(-199.4, 47.58) * mm});
            skLineSegment(sketch, "E126.top", {"start": v(-188.8, 36.98) * mm, "end": v(-199.4, 36.98) * mm});
            skLineSegment(sketch, "E126.left", {"start": v(-188.8, 47.58) * mm, "end": v(-188.8, 36.98) * mm});
            skLineSegment(sketch, "E126.right", {"start": v(-199.4, 47.58) * mm, "end": v(-199.4, 36.98) * mm});
            skSolve(sketch);
        }
        {
            var Q0;
            Q0=makeQuery(id+"F6.imprint","IMPRINT",FACE,{"disambiguationData":[TD([[makeQuery(id+"F6.imprint","IMPRINT",EDGE,{"derivedFrom":sQuery(id+"F6.wireOp",EDGE,"E70.bottom")}),1.0]])]});
            var Q1;
            Q1=makeQuery(id+"F6.imprint","IMPRINT",FACE,{"disambiguationData":[TD([[makeQuery(id+"F6.imprint","IMPRINT",EDGE,{"derivedFrom":sQuery(id+"F6.wireOp",EDGE,"E73.bottom")}),1.0]])]});
            var Q2;
            Q2=makeQuery(id+"F6.imprint","IMPRINT",FACE,{"disambiguationData":[TD([[makeQuery(id+"F6.imprint","IMPRINT",EDGE,{"derivedFrom":sQuery(id+"F6.wireOp",EDGE,"E75.bottom")}),1.0]])]});
            var Q3;
            Q3=makeQuery(id+"F6.imprint","IMPRINT",FACE,{"disambiguationData":[TD([[makeQuery(id+"F6.imprint","IMPRINT",EDGE,{"derivedFrom":sQuery(id+"F6.wireOp",EDGE,"E77.bottom")}),1.0]])]});
            var Q4;
            Q4=makeQuery(id+"F6.imprint","IMPRINT",FACE,{"disambiguationData":[TD([[makeQuery(id+"F6.imprint","IMPRINT",EDGE,{"derivedFrom":sQuery(id+"F6.wireOp",EDGE,"E79.bottom")}),1.0]])]});
            var Q5;
            Q5=makeQuery(id+"F6.imprint","IMPRINT",FACE,{"disambiguationData":[TD([[makeQuery(id+"F6.imprint","IMPRINT",EDGE,{"derivedFrom":sQuery(id+"F6.wireOp",EDGE,"E81.bottom")}),1.0]])]});
            var Q6;
            Q6=makeQuery(id+"F6.imprint","IMPRINT",FACE,{"disambiguationData":[TD([[makeQuery(id+"F6.imprint","IMPRINT",EDGE,{"derivedFrom":sQuery(id+"F6.wireOp",EDGE,"E83.bottom")}),1.0]])]});
            var Q7;
            Q7=makeQuery(id+"F6.imprint","IMPRINT",FACE,{"disambiguationData":[TD([[makeQuery(id+"F6.imprint","IMPRINT",EDGE,{"derivedFrom":sQuery(id+"F6.wireOp",EDGE,"E85.bottom")}),1.0]])]});
            var Q8;
            Q8=makeQuery(id+"F6.imprint","IMPRINT",FACE,{"disambiguationData":[TD([[makeQuery(id+"F6.imprint","IMPRINT",EDGE,{"derivedFrom":sQuery(id+"F6.wireOp",EDGE,"E87.bottom")}),1.0]])]});
            var Q9;
            Q9=makeQuery(id+"F6.imprint","IMPRINT",FACE,{"disambiguationData":[TD([[makeQuery(id+"F6.imprint","IMPRINT",EDGE,{"derivedFrom":sQuery(id+"F6.wireOp",EDGE,"E107.bottom")}),1.0]])]});
            var Q10;
            Q10=makeQuery(id+"F6.imprint","IMPRINT",FACE,{"disambiguationData":[TD([[makeQuery(id+"F6.imprint","IMPRINT",EDGE,{"derivedFrom":sQuery(id+"F6.wireOp",EDGE,"E105.bottom")}),1.0]])]});
            var Q11;
            Q11=makeQuery(id+"F6.imprint","IMPRINT",FACE,{"disambiguationData":[TD([[makeQuery(id+"F6.imprint","IMPRINT",EDGE,{"derivedFrom":sQuery(id+"F6.wireOp",EDGE,"E103.bottom")}),1.0]])]});
            var Q12;
            Q12=makeQuery(id+"F6.imprint","IMPRINT",FACE,{"disambiguationData":[TD([[makeQuery(id+"F6.imprint","IMPRINT",EDGE,{"derivedFrom":sQuery(id+"F6.wireOp",EDGE,"E101.bottom")}),1.0]])]});
            var Q13;
            Q13=makeQuery(id+"F6.imprint","IMPRINT",FACE,{"disambiguationData":[TD([[makeQuery(id+"F6.imprint","IMPRINT",EDGE,{"derivedFrom":sQuery(id+"F6.wireOp",EDGE,"E99.bottom")}),1.0]])]});
            var Q14;
            Q14=makeQuery(id+"F6.imprint","IMPRINT",FACE,{"disambiguationData":[TD([[makeQuery(id+"F6.imprint","IMPRINT",EDGE,{"derivedFrom":sQuery(id+"F6.wireOp",EDGE,"E97.bottom")}),1.0]])]});
            var Q15;
            Q15=makeQuery(id+"F6.imprint","IMPRINT",FACE,{"disambiguationData":[TD([[makeQuery(id+"F6.imprint","IMPRINT",EDGE,{"derivedFrom":sQuery(id+"F6.wireOp",EDGE,"E95.bottom")}),1.0]])]});
            var Q16;
            Q16=makeQuery(id+"F6.imprint","IMPRINT",FACE,{"disambiguationData":[TD([[makeQuery(id+"F6.imprint","IMPRINT",EDGE,{"derivedFrom":sQuery(id+"F6.wireOp",EDGE,"E93.bottom")}),1.0]])]});
            var Q17;
            Q17=makeQuery(id+"F6.imprint","IMPRINT",FACE,{"disambiguationData":[TD([[makeQuery(id+"F6.imprint","IMPRINT",EDGE,{"derivedFrom":sQuery(id+"F6.wireOp",EDGE,"E91.bottom")}),1.0]])]});
            var Q18;
            Q18=makeQuery(id+"F6.imprint","IMPRINT",FACE,{"disambiguationData":[TD([[makeQuery(id+"F6.imprint","IMPRINT",EDGE,{"derivedFrom":sQuery(id+"F6.wireOp",EDGE,"E109.bottom")}),1.0]])]});
            var Q19;
            Q19=makeQuery(id+"F6.imprint","IMPRINT",FACE,{"disambiguationData":[TD([[makeQuery(id+"F6.imprint","IMPRINT",EDGE,{"derivedFrom":sQuery(id+"F6.wireOp",EDGE,"E111.bottom")}),1.0]])]});
            var Q20;
            Q20=makeQuery(id+"F6.imprint","IMPRINT",FACE,{"disambiguationData":[TD([[makeQuery(id+"F6.imprint","IMPRINT",EDGE,{"derivedFrom":sQuery(id+"F6.wireOp",EDGE,"E113.bottom")}),1.0]])]});
            var Q21;
            Q21=makeQuery(id+"F6.imprint","IMPRINT",FACE,{"disambiguationData":[TD([[makeQuery(id+"F6.imprint","IMPRINT",EDGE,{"derivedFrom":sQuery(id+"F6.wireOp",EDGE,"E115.bottom")}),1.0]])]});
            var Q22;
            Q22=makeQuery(id+"F6.imprint","IMPRINT",FACE,{"disambiguationData":[TD([[makeQuery(id+"F6.imprint","IMPRINT",EDGE,{"derivedFrom":sQuery(id+"F6.wireOp",EDGE,"E117.bottom")}),1.0]])]});
            var Q23;
            Q23=makeQuery(id+"F6.imprint","IMPRINT",FACE,{"disambiguationData":[TD([[makeQuery(id+"F6.imprint","IMPRINT",EDGE,{"derivedFrom":sQuery(id+"F6.wireOp",EDGE,"E119.bottom")}),1.0]])]});
            var Q24;
            Q24=makeQuery(id+"F6.imprint","IMPRINT",FACE,{"disambiguationData":[TD([[makeQuery(id+"F6.imprint","IMPRINT",EDGE,{"derivedFrom":sQuery(id+"F6.wireOp",EDGE,"E121.bottom")}),1.0]])]});
            var Q25;
            Q25=makeQuery(id+"F6.imprint","IMPRINT",FACE,{"disambiguationData":[TD([[makeQuery(id+"F6.imprint","IMPRINT",EDGE,{"derivedFrom":sQuery(id+"F6.wireOp",EDGE,"E123.bottom")}),1.0]])]});
            var Q26;
            Q26=makeQuery(id+"F6.imprint","IMPRINT",FACE,{"disambiguationData":[TD([[makeQuery(id+"F6.imprint","IMPRINT",EDGE,{"derivedFrom":sQuery(id+"F6.wireOp",EDGE,"E126.bottom")}),1.0]])]});
            extrude(context, id + "F7", {"entities" : qUnion([Q0, Q1, Q2, Q3, Q4, Q5, Q6, Q7, Q8, Q9, Q10, Q11, Q12, Q13, Q14, Q15, Q16, Q17, Q18, Q19, Q20, Q21, Q22, Q23, Q24, Q25, Q26]), "operationType" : NewBodyOperationType.REMOVE, "depth" : 20 * mm});
        }
        {
            var Q0;
            Q0=makeQuery(id+"F1.opExtrude","SWEPT_EDGE",EDGE,{"disambiguationData":[OSD([sQuery(id+"F0.wireOp",EDGE,"E1"),sQuery(id+"F0.wireOp",EDGE,"E2")])]});
            var Q1;
            Q1=makeQuery(id+"F1.opExtrude","SWEPT_EDGE",EDGE,{"disambiguationData":[OSD([sQuery(id+"F0.wireOp",EDGE,"E4"),sQuery(id+"F0.wireOp",EDGE,"E5")])]});
            fillet(context, id + "F8", {"entities" : qUnion([Q0, Q1]), "radius" : 10 * mm, "tangentPropagation" : true, "allowEdgeOverflow" : false});
        }
    });
